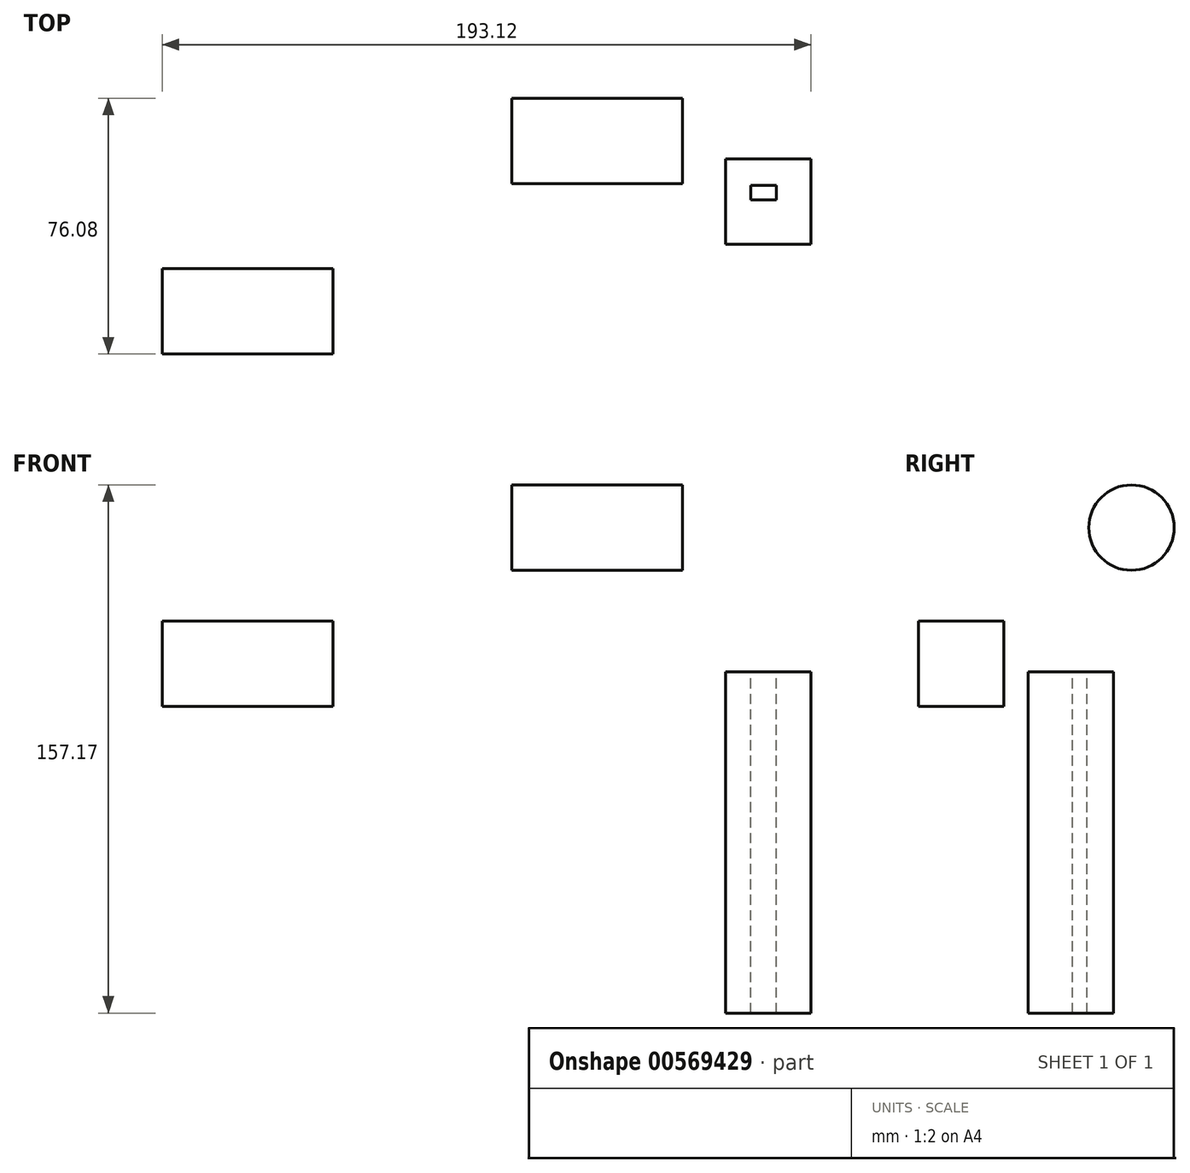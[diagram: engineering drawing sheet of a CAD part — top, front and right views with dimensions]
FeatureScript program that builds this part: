
annotation { "Feature Type Name" : "Feature", "Feature Type Description" : "" }
export const myFeature = defineFeature(function(context is Context, id is Id, definition is map)
    precondition{}
    {
        {
            var Q0;
            Q0=qCreatedBy(makeId("Front.planeOp"),FACE);
            var sketch = newSketch(context, id + "F0", { "sketchPlane" : qUnion([Q0])});
            skLineSegment(sketch, "E0.bottom", {"start": v(-129.42, 15.07) * mm, "end": v(-78.62, 15.07) * mm});
            skLineSegment(sketch, "E0.top", {"start": v(-129.42, -10.33) * mm, "end": v(-78.62, -10.33) * mm});
            skLineSegment(sketch, "E0.left", {"start": v(-129.42, 15.07) * mm, "end": v(-129.42, -10.33) * mm});
            skLineSegment(sketch, "E0.right", {"start": v(-78.62, 15.07) * mm, "end": v(-78.62, -10.33) * mm});
            skSolve(sketch);
        }
        {
            var Q0;
            Q0=makeQuery(id+"F0.imprint","IMPRINT",FACE,{"disambiguationData":[TD([[makeQuery(id+"F0.imprint","IMPRINT",EDGE,{"derivedFrom":sQuery(id+"F0.wireOp",EDGE,"E0.bottom")}),-1.0]])]});
            extrude(context, id + "F1", {"entities" : qUnion([Q0]), "depth" : 25.4 * mm, "offsetDistance" : 25.4 * mm});
        }
        {
            var Q0;
            Q0=qCreatedBy(makeId("Top.planeOp"),FACE);
            var sketch = newSketch(context, id + "F2", { "sketchPlane" : qUnion([Q0])});
            skLineSegment(sketch, "E1.bottom", {"start": v(38.3, 32.64) * mm, "end": v(63.7, 32.64) * mm});
            skLineSegment(sketch, "E1.top", {"start": v(38.3, 7.24) * mm, "end": v(63.7, 7.24) * mm});
            skLineSegment(sketch, "E1.left", {"start": v(38.3, 32.64) * mm, "end": v(38.3, 7.24) * mm});
            skLineSegment(sketch, "E1.right", {"start": v(63.7, 32.64) * mm, "end": v(63.7, 7.24) * mm});
            skLineSegment(sketch, "E2.bottom", {"start": v(45.78, 20.44) * mm, "end": v(53.38, 20.44) * mm});
            skLineSegment(sketch, "E2.top", {"start": v(45.78, 24.74) * mm, "end": v(53.38, 24.74) * mm});
            skLineSegment(sketch, "E2.left", {"start": v(45.78, 20.44) * mm, "end": v(45.78, 24.74) * mm});
            skLineSegment(sketch, "E2.right", {"start": v(53.38, 20.44) * mm, "end": v(53.38, 24.74) * mm});
            skSolve(sketch);
        }
        {
            var Q0;
            Q0=makeQuery(id+"F2.imprint","IMPRINT",FACE,{"disambiguationData":[TD([[makeQuery(id+"F2.imprint","IMPRINT",EDGE,{"derivedFrom":sQuery(id+"F2.wireOp",EDGE,"E1.bottom")}),-1.0]])]});
            extrude(context, id + "F3", {"entities" : qUnion([Q0]), "oppositeDirection" : true, "depth" : 101.6 * mm, "offsetDistance" : 25.4 * mm});
        }
        {
            var Q0;
            Q0=qCreatedBy(makeId("Right.planeOp"),FACE);
            var sketch = newSketch(context, id + "F4", { "sketchPlane" : qUnion([Q0])});
            skCircle(sketch, "E3", {"center": v(37.98, 42.87) * mm, "radius": 12.7 * mm});
            skSolve(sketch);
        }
        {
            var Q0;
            Q0 = qSketchRegion(id + "F4", true);
            extrude(context, id + "F5", {"entities" : qUnion([Q0]), "depth" : 25.4 * mm, "offsetDistance" : 25.4 * mm});
        }
        {
            var Q0;
            Q0 = qSketchRegion(id + "F4", true);
            extrude(context, id + "F6", {"entities" : qUnion([Q0]), "operationType" : NewBodyOperationType.ADD, "oppositeDirection" : true, "depth" : 25.4 * mm, "offsetDistance" : 25.4 * mm});
        }
    });
